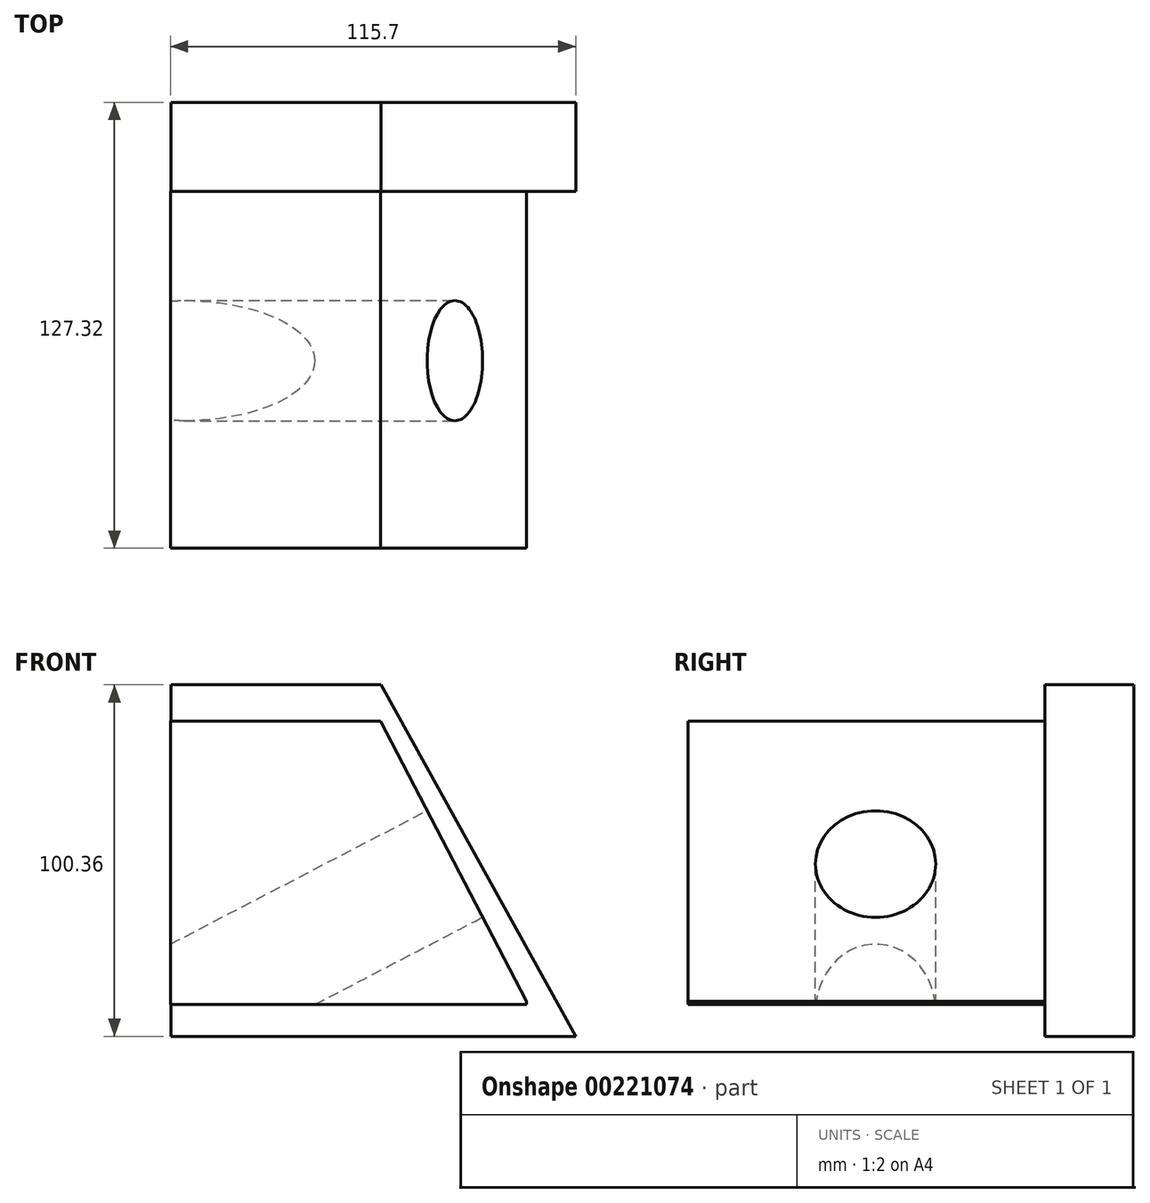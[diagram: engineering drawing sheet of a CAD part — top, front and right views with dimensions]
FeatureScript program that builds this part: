
annotation { "Feature Type Name" : "Feature", "Feature Type Description" : "" }
export const myFeature = defineFeature(function(context is Context, id is Id, definition is map)
    precondition{}
    {
        {
            var Q0;
            Q0=qCreatedBy(makeId("Right.planeOp"),FACE);
            var sketch = newSketch(context, id + "F0", { "sketchPlane" : qUnion([Q0])});
            skLineSegment(sketch, "E0.bottom", {"start": v(-53.57, 53.37) * mm, "end": v(48.35, 53.37) * mm});
            skLineSegment(sketch, "E0.top", {"start": v(-53.57, -53.76) * mm, "end": v(48.35, -53.76) * mm});
            skLineSegment(sketch, "E0.left", {"start": v(-53.57, 53.37) * mm, "end": v(-53.57, -53.76) * mm});
            skLineSegment(sketch, "E0.right", {"start": v(48.35, 53.37) * mm, "end": v(48.35, -53.76) * mm});
            skSolve(sketch);
        }
        {
            var Q0;
            Q0 = qSketchRegion(id + "F0", true);
            extrude(context, id + "F1", {"entities" : qUnion([Q0]), "oppositeDirection" : true, "depth" : 101.6 * mm});
        }
        {
            var Q0;
            Q0=makeQuery(id+"F1.opExtrude","SWEPT_FACE",FACE,{"disambiguationData":[OSD([sQuery(id+"F0.wireOp",EDGE,"E0.left")])]});
            var sketch = newSketch(context, id + "F2", { "sketchPlane" : qUnion([Q0])});
            skLineSegment(sketch, "E1", {"start": v(-55.26, 53.37) * mm, "end": v(9.4, -70.94) * mm});
            skLineSegment(sketch, "E2", {"start": v(9.4, -70.94) * mm, "end": v(13.07, 68.62) * mm});
            skLineSegment(sketch, "E3", {"start": v(13.07, 68.62) * mm, "end": v(-55.26, 53.37) * mm});
            skSolve(sketch);
        }
        {
            var Q0;
            Q0 = qSketchRegion(id + "F2", true);
            extrude(context, id + "F3", {"entities" : qUnion([Q0]), "operationType" : NewBodyOperationType.REMOVE, "endBound" : BoundingType.THROUGH_ALL, "oppositeDirection" : true, "depth" : 25.4 * mm});
        }
        {
            var Q0;
            Q0=makeQuery(id+"F1.opExtrude","SWEPT_FACE",FACE,{"disambiguationData":[OSD([sQuery(id+"F0.wireOp",EDGE,"E0.left")])]});
            var sketch = newSketch(context, id + "F4", { "sketchPlane" : qUnion([Q0])});
            skLineSegment(sketch, "E4", {"start": v(-122.05, 27.12) * mm, "end": v(-16.08, 27.12) * mm});
            skLineSegment(sketch, "E5", {"start": v(-16.08, 27.12) * mm, "end": v(-20.71, 66.11) * mm});
            skLineSegment(sketch, "E6", {"start": v(-20.71, 66.11) * mm, "end": v(-121.28, 53.37) * mm});
            skLineSegment(sketch, "E7", {"start": v(-121.28, 53.37) * mm, "end": v(-122.05, 27.12) * mm});
            skSolve(sketch);
        }
        {
            var Q0;
            Q0 = qSketchRegion(id + "F4", true);
            extrude(context, id + "F5", {"entities" : qUnion([Q0]), "operationType" : NewBodyOperationType.REMOVE, "endBound" : BoundingType.THROUGH_ALL, "oppositeDirection" : true, "depth" : 25.4 * mm});
        }
        {
            var Q0;
            Q0=makeQuery(id+"F3.boolean.opBoolean","COPY",FACE,{"derivedFrom":makeQuery(id+"F3.opExtrude","SWEPT_FACE",FACE,{"disambiguationData":[OSD([sQuery(id+"F2.wireOp",EDGE,"E1")])]})});
            var sketch = newSketch(context, id + "F6", { "sketchPlane" : qUnion([Q0])});
            skCircle(sketch, "E8", {"center": v(0, -2.65) * mm, "radius": 17.16 * mm});
            skSolve(sketch);
        }
        {
            var Q0;
            Q0 = qSketchRegion(id + "F6", true);
            extrude(context, id + "F7", {"entities" : qUnion([Q0]), "operationType" : NewBodyOperationType.REMOVE, "endBound" : BoundingType.THROUGH_ALL, "oppositeDirection" : true, "depth" : 203.2 * mm});
        }
        {
            var Q0;
            Q0=makeQuery(id+"F1.opExtrude","SWEPT_FACE",FACE,{"disambiguationData":[OSD([sQuery(id+"F0.wireOp",EDGE,"E0.right")])]});
            var sketch = newSketch(context, id + "F8", { "sketchPlane" : qUnion([Q0])});
            skLineSegment(sketch, "E9", {"start": v(101.6, 27.12) * mm, "end": v(41.6, 27.12) * mm});
            skLineSegment(sketch, "E10", {"start": v(41.6, 27.12) * mm, "end": v(4.12, -44.94) * mm});
            skLineSegment(sketch, "E11", {"start": v(4.12, -44.94) * mm, "end": v(0, -52.86) * mm});
            skLineSegment(sketch, "E12", {"start": v(0, -52.86) * mm, "end": v(101.6, -53.76) * mm});
            skLineSegment(sketch, "E13", {"start": v(101.6, -53.76) * mm, "end": v(101.6, 27.12) * mm});
            skSolve(sketch);
        }
        {
            var Q0;
            Q0=makeQuery(id+"F8.imprint","IMPRINT",FACE,{"disambiguationData":[TD([[makeQuery(id+"F8.imprint","IMPRINT",EDGE,{"derivedFrom":sQuery(id+"F8.wireOp",EDGE,"E9")}),1.0]])]});
            var sketch = newSketch(context, id + "F9", { "sketchPlane" : qUnion([Q0])});
            skLineSegment(sketch, "E14", {"start": v(101.43, 37.54) * mm, "end": v(101.43, -54.22) * mm});
            skLineSegment(sketch, "E15", {"start": v(101.43, -54.22) * mm, "end": v(101.43, -62.82) * mm});
            skLineSegment(sketch, "E16", {"start": v(101.43, -62.82) * mm, "end": v(-14.1, -62.82) * mm});
            skLineSegment(sketch, "E17", {"start": v(101.43, 37.54) * mm, "end": v(41.52, 37.54) * mm});
            skLineSegment(sketch, "E18", {"start": v(41.52, 37.54) * mm, "end": v(-14.1, -62.82) * mm});
            skSolve(sketch);
        }
        {
            var Q0;
            Q0 = qSketchRegion(id + "F9", true);
            extrude(context, id + "F10", {"entities" : qUnion([Q0]), "operationType" : NewBodyOperationType.ADD, "depth" : 25.4 * mm});
        }
    });
